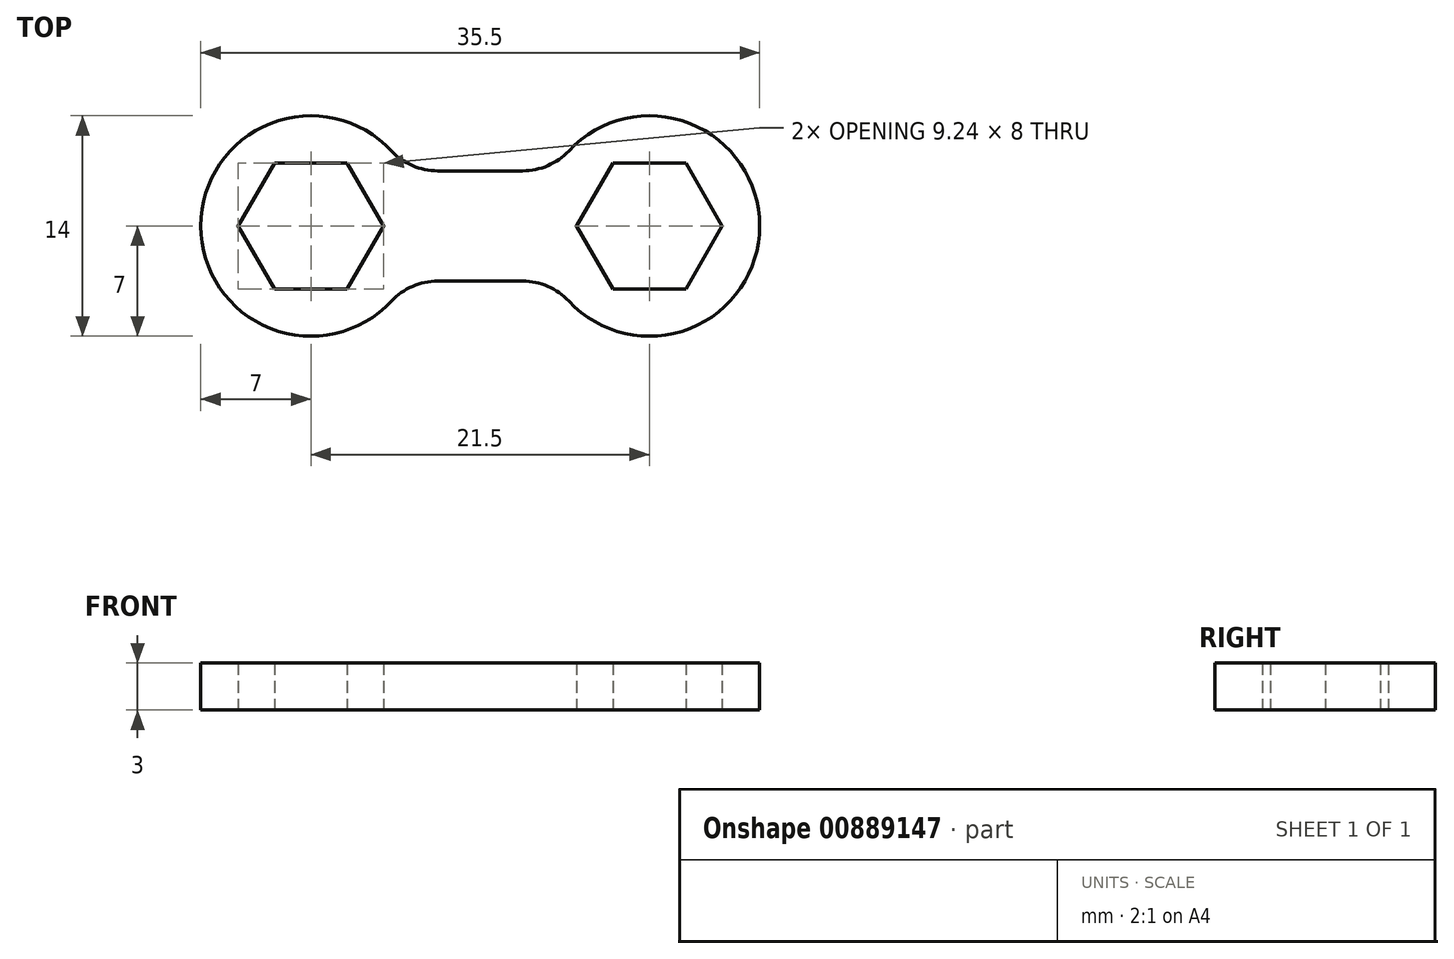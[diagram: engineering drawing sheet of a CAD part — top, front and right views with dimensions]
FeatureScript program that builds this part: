
annotation { "Feature Type Name" : "Feature", "Feature Type Description" : "" }
export const myFeature = defineFeature(function(context is Context, id is Id, definition is map)
    precondition{}
    {
        {
            var Q0;
            Q0=qCreatedBy(makeId("Top.planeOp"),FACE);
            var sketch = newSketch(context, id + "F0", { "sketchPlane" : qUnion([Q0])});
            skCircle(sketch, "E0.cCircle", {"center": v(-10.75, 0) * mm, "radius": 4 * mm, "construction": true});
            skLineSegment(sketch, "E0.0", {"start": v(-8.44, -4) * mm, "end": v(-13.06, -4) * mm});
            skLineSegment(sketch, "E0.1", {"start": v(-13.06, -4) * mm, "end": v(-15.37, 0) * mm});
            skLineSegment(sketch, "E0.2", {"start": v(-15.37, 0) * mm, "end": v(-13.06, 4) * mm});
            skLineSegment(sketch, "E0.3", {"start": v(-13.06, 4) * mm, "end": v(-8.44, 4) * mm});
            skLineSegment(sketch, "E0.4", {"start": v(-8.44, 4) * mm, "end": v(-6.13, 0) * mm});
            skLineSegment(sketch, "E0.5", {"start": v(-6.13, 0) * mm, "end": v(-8.44, -4) * mm});
            skPoint(sketch, "E0.0.midPoint", {"position": v(-10.75, -4) * mm});
            skCircle(sketch, "E1.cCircle", {"center": v(10.75, 0) * mm, "radius": 4 * mm, "construction": true});
            skLineSegment(sketch, "E1.0", {"start": v(13.06, -4) * mm, "end": v(8.44, -4) * mm});
            skLineSegment(sketch, "E1.1", {"start": v(8.44, -4) * mm, "end": v(6.13, 0) * mm});
            skLineSegment(sketch, "E1.2", {"start": v(6.13, 0) * mm, "end": v(8.44, 4) * mm});
            skLineSegment(sketch, "E1.3", {"start": v(8.44, 4) * mm, "end": v(13.06, 4) * mm});
            skLineSegment(sketch, "E1.4", {"start": v(13.06, 4) * mm, "end": v(15.37, 0) * mm});
            skLineSegment(sketch, "E1.5", {"start": v(15.37, 0) * mm, "end": v(13.06, -4) * mm});
            skPoint(sketch, "E1.0.midPoint", {"position": v(10.75, -4) * mm});
            skLineSegment(sketch, "E2", {"start": v(-10.75, 0) * mm, "end": v(10.75, 0) * mm, "construction": true});
            skArc(sketch, "E3", {"start": v(-5.63, 4.77) * mm, "mid": v(-17.75, 0) * mm, "end": v(-5.63, -4.77) * mm});
            skArc(sketch, "E4", {"start": v(5.63, -4.77) * mm, "mid": v(17.75, 0) * mm, "end": v(5.63, 4.77) * mm});
            skLineSegment(sketch, "E5", {"start": v(-2.7, 3.5) * mm, "end": v(2.7, 3.5) * mm});
            skLineSegment(sketch, "E6", {"start": v(-2.7, -3.5) * mm, "end": v(2.7, -3.5) * mm});
            skLineSegment(sketch, "E7", {"start": v(0, 3.5) * mm, "end": v(0, -3.5) * mm, "construction": true});
            skPoint(sketch, "E8.visualSharp", {"position": v(-4.69, 3.5) * mm});
            skArc(sketch, "E8.filletArc", {"start": v(-5.63, 4.77) * mm, "mid": v(-4.3, 3.83) * mm, "end": v(-2.7, 3.5) * mm});
            skPoint(sketch, "E9.visualSharp", {"position": v(4.69, 3.5) * mm});
            skArc(sketch, "E9.filletArc", {"start": v(2.7, 3.5) * mm, "mid": v(4.3, 3.83) * mm, "end": v(5.63, 4.77) * mm});
            skPoint(sketch, "E10.visualSharp", {"position": v(4.69, -3.5) * mm});
            skArc(sketch, "E10.filletArc", {"start": v(5.63, -4.77) * mm, "mid": v(4.3, -3.83) * mm, "end": v(2.7, -3.5) * mm});
            skPoint(sketch, "E11.visualSharp", {"position": v(-4.69, -3.5) * mm});
            skArc(sketch, "E11.filletArc", {"start": v(-2.7, -3.5) * mm, "mid": v(-4.3, -3.83) * mm, "end": v(-5.63, -4.77) * mm});
            skSolve(sketch);
        }
        {
            var Q0;
            Q0 = qSketchRegion(id + "F0", true);
            extrude(context, id + "F1", {"entities" : qUnion([Q0]), "depth" : 3 * mm, "offsetDistance" : 25 * mm});
        }
    });
